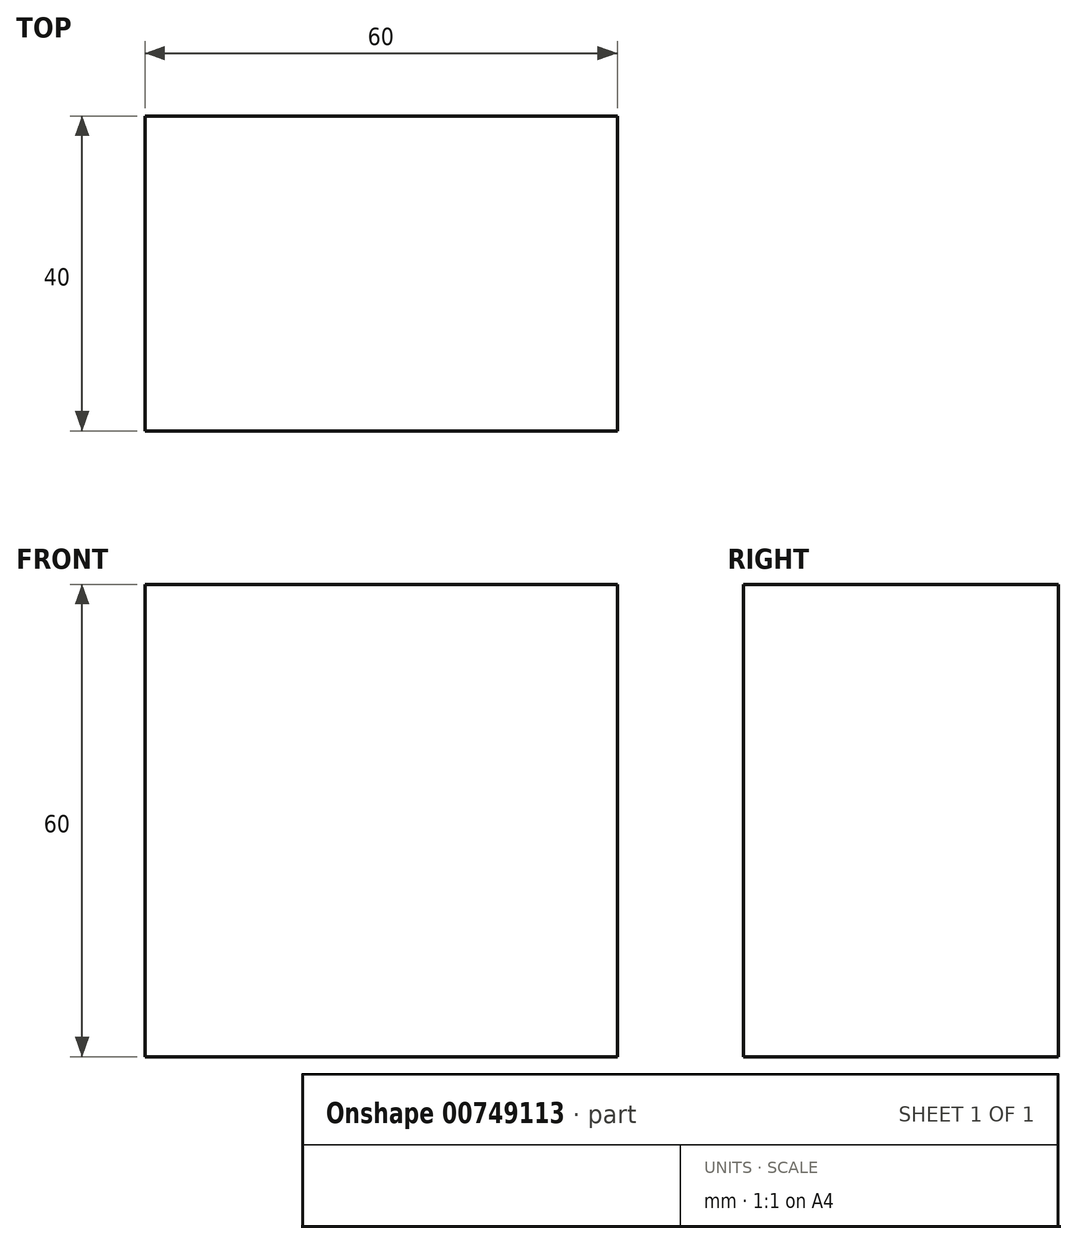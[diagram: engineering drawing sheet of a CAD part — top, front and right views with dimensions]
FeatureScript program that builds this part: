
annotation { "Feature Type Name" : "Feature", "Feature Type Description" : "" }
export const myFeature = defineFeature(function(context is Context, id is Id, definition is map)
    precondition{}
    {
        {
            var Q0;
            Q0=qCreatedBy(makeId("Front.planeOp"),FACE);
            var sketch = newSketch(context, id + "F0", { "sketchPlane" : qUnion([Q0])});
            skLineSegment(sketch, "E0", {"start": v(0, 60) * mm, "end": v(0, 0) * mm});
            skLineSegment(sketch, "E1", {"start": v(0, 0) * mm, "end": v(60, 0) * mm});
            skLineSegment(sketch, "E2", {"start": v(60, 0) * mm, "end": v(60, 60) * mm});
            skLineSegment(sketch, "E3", {"start": v(60, 60) * mm, "end": v(0, 60) * mm});
            skSolve(sketch);
        }
        {
            var Q0;
            Q0=makeQuery(id+"F0.imprint","IMPRINT",FACE,{"disambiguationData":[TD([[makeQuery(id+"F0.imprint","IMPRINT",EDGE,{"derivedFrom":sQuery(id+"F0.wireOp",EDGE,"E0")}),1.0]])]});
            extrude(context, id + "F1", {"entities" : qUnion([Q0]), "depth" : 40 * mm, "offsetDistance" : 25 * mm});
        }
    });
